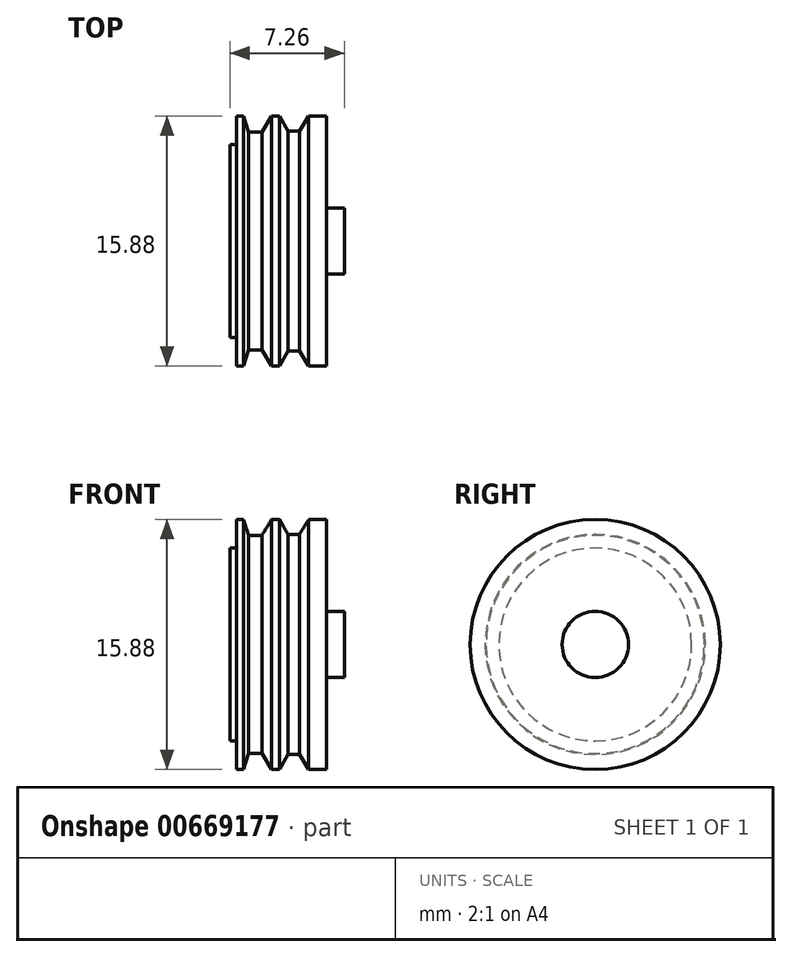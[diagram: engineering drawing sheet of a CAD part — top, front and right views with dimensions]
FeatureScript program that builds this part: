
annotation { "Feature Type Name" : "Feature", "Feature Type Description" : "" }
export const myFeature = defineFeature(function(context is Context, id is Id, definition is map)
    precondition{}
    {
        {
            var Q0;
            Q0=qCreatedBy(makeId("Front.planeOp"),FACE);
            var sketch = newSketch(context, id + "F0", { "sketchPlane" : qUnion([Q0])});
            skLineSegment(sketch, "E0", {"start": v(0, 0) * mm, "end": v(0, 33.02) * mm});
            skLineSegment(sketch, "E1", {"start": v(0, 33.02) * mm, "end": v(-3.5, 33.02) * mm});
            skLineSegment(sketch, "E2", {"start": v(-3.5, 33.02) * mm, "end": v(-5.13, 29.4) * mm});
            skLineSegment(sketch, "E3", {"start": v(-5.13, 29.4) * mm, "end": v(-7.32, 29.4) * mm});
            skLineSegment(sketch, "E4", {"start": v(-7.32, 29.4) * mm, "end": v(-8.74, 32.95) * mm});
            skLineSegment(sketch, "E5", {"start": v(-8.74, 32.95) * mm, "end": v(-9.73, 32.95) * mm});
            skLineSegment(sketch, "E6", {"start": v(-9.73, 32.95) * mm, "end": v(-11.57, 29.4) * mm});
            skLineSegment(sketch, "E7", {"start": v(-11.57, 29.4) * mm, "end": v(-13.62, 29.4) * mm});
            skLineSegment(sketch, "E8", {"start": v(-13.62, 29.4) * mm, "end": v(-14.83, 32.95) * mm});
            skLineSegment(sketch, "E9", {"start": v(-14.83, 32.95) * mm, "end": v(-16.24, 32.95) * mm});
            skLineSegment(sketch, "E10", {"start": v(0, 7.94) * mm, "end": v(-1.13, 7.94) * mm});
            skLineSegment(sketch, "E11", {"start": v(-1.13, 7.94) * mm, "end": v(-1.73, 6.99) * mm});
            skLineSegment(sketch, "E12", {"start": v(-1.73, 6.99) * mm, "end": v(-2.44, 6.99) * mm});
            skLineSegment(sketch, "E13", {"start": v(-2.44, 6.99) * mm, "end": v(-2.98, 7.94) * mm});
            skLineSegment(sketch, "E14", {"start": v(-2.98, 7.94) * mm, "end": v(-3.48, 7.94) * mm});
            skLineSegment(sketch, "E15", {"start": v(-3.48, 7.94) * mm, "end": v(-4.1, 6.93) * mm});
            skLineSegment(sketch, "E16", {"start": v(-4.1, 6.93) * mm, "end": v(-4.94, 6.93) * mm});
            skLineSegment(sketch, "E17", {"start": v(-4.94, 6.93) * mm, "end": v(-5.27, 7.94) * mm});
            skLineSegment(sketch, "E18", {"start": v(-5.27, 7.94) * mm, "end": v(-5.72, 7.94) * mm});
            skLineSegment(sketch, "E19", {"start": v(-5.72, 7.94) * mm, "end": v(-5.72, 6.13) * mm});
            skLineSegment(sketch, "E20", {"start": v(-5.72, 6.13) * mm, "end": v(-6.13, 6.13) * mm});
            skLineSegment(sketch, "E21", {"start": v(-6.13, 6.13) * mm, "end": v(-6.13, 0) * mm});
            skLineSegment(sketch, "E22", {"start": v(0, 2.1) * mm, "end": v(1.13, 2.1) * mm});
            skLineSegment(sketch, "E23", {"start": v(1.13, 2.1) * mm, "end": v(1.13, 0) * mm});
            skPoint(sketch, "E24.start.orphan", {"position": v(-2.98, 6.99) * mm});
            skLineSegment(sketch, "E25", {"start": v(-6.13, 0) * mm, "end": v(1.13, 0) * mm});
            skSolve(sketch);
        }
        {
            var Q0;
            Q0 = qSketchRegion(id + "F0", true);
            var Q1;
            Q1=sQuery(id+"F0.wireOp",EDGE,"E25");
            revolve(context, id + "F1", {"entities" : qUnion([Q0]), "axis" : qUnion([Q1]), "revolveType" : RevolveType.FULL});
        }
    });
